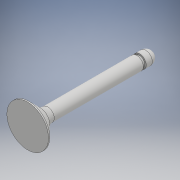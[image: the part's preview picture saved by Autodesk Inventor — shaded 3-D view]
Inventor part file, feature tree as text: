
AUTODESK INVENTOR PART (.ipt)
format: ipt  version: 2018 (Build 220112000, 112)  size: 127,488 bytes
history: native  units: mm
features: revolve x1, sketch x1
ambient origin geometry x8: Origin, YZ Plane, XZ Plane, XY Plane, X Axis, Y Axis, Z Axis, Center Point
bodies: Solid1 (feature_tree)
feature tree (2):
  revolve  "Revolution1"  [1 undecoded]
  sketch  "Sketch1"  dims[d1=4.75mm d2=1.5mm d3=0.3mm d4=45.0deg d5=1.5mm d6=1.15mm d8=0.65mm d9=1.4mm d10=27.0mm d11=2.5mm d12=90.0deg]
note: 1 required parameter value undecoded (feature->parameter linkage not recoverable at this tier; creation-order binding heuristic only, values carry confidence <= 0.55)
